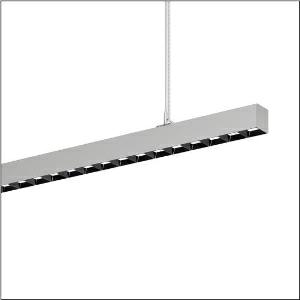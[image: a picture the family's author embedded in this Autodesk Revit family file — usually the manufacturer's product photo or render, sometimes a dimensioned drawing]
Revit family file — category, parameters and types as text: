
# Revit family: silica_r__21_51mx31tctds_9889
name_source: partatom
category: Lighting Fixtures
units: mm (PartAtom-declared; Revit-internal decimal feet)

## family parameters
Cut with Voids When Loaded = No
Host = Face
Light Source = No
Part Type = Normal
Room Calculation Point = No
Round Connector Dimension = Use Diameter
Shared = No

## types (1)
- --- (1 x LED, 15550 lm, 133.9 W, 6500K)
    Apparent Load = 134 VA
    CIE Flux Codes = 85 99 100 60 100
    Color Rendering = 80
    Color Temperature = 6500K
    Default Elevation = 1800 mm
    Description = Silica® 21, office luminaire, primary light control with darklight reflector, of PMMA, black, CAT 2 (L<= 3000cd/m²), light emission: direct/indirect distribution, primary light characteristic: symmetric, installation type: suspended mounting, LED, rated luminous flux: 15.550lm, luminous efficacy: 111lm/W, light colour: 8tw, colour temperature: 2700..6500K, control gear: ECG DALI, with terminal, 3+2-pole, max. 2.5mm², mains connection: 220..240V, AC, 50/60Hz, rated input power: 140.6W, luminaire housing, of aluminium, metallic grey (RAL 9006), length: 3.004mm, width: 53mm, height: 53mm, protection rating (complete): IP20, insulation class (complete): insulation class I (protective earthing), certification: CE, permissible operating ambient temperature: 0..+35°C, standard: EN 50419, packaging unit: 1 piece
    Height = 53 mm
    Lamp = 1 x LED
    Lamp Light Flux = 15550 lm
    Lamp Power = 133.9 W
    Lamp count = 1
    Length = 3004 mm
    Luminous efficacy = 116 lm/W
    Manufacturer = Siteco
    ModVariant = No
    Model = 51MX31TCTDS
    Mounting Place = Ceiling
    Mounting Type = Pendant
    Number of Poles = 1
    OnlyDefault = Yes
    Power Factor = 1
    Product Name = Silica® 21
    Product group = office luminaire | ceiling pendant
    ProductGroupID = 902
    Protection Class = Protection class I
    Protection Degree = IP 20
    RLX_Detail_Level = 1
    RLX_Emergency_Light_Flux = 0 lm
    RLX_Emergency_Type = 0
    RLX_Emergency_Type_DB = No
    RlxData = <blob elided: 61873 chars, md5=9223cb3d>
    Socket = socket
    Standby Power = 0 W
    System Light Flux = 15550 lm
    System Power = 134 W
    Type Comments = individual setting
    Type Image = l_1335859.jpg
    URL = http://relux.com
    VarID = @adj_109663
    Voltage = 0 V
    Weight = 0.00 kg
    Width = 53 mm

## geometry (parser evidence)
native form markers: Blend x4, Sweep x14
no freeform markers — native parametric forms only
